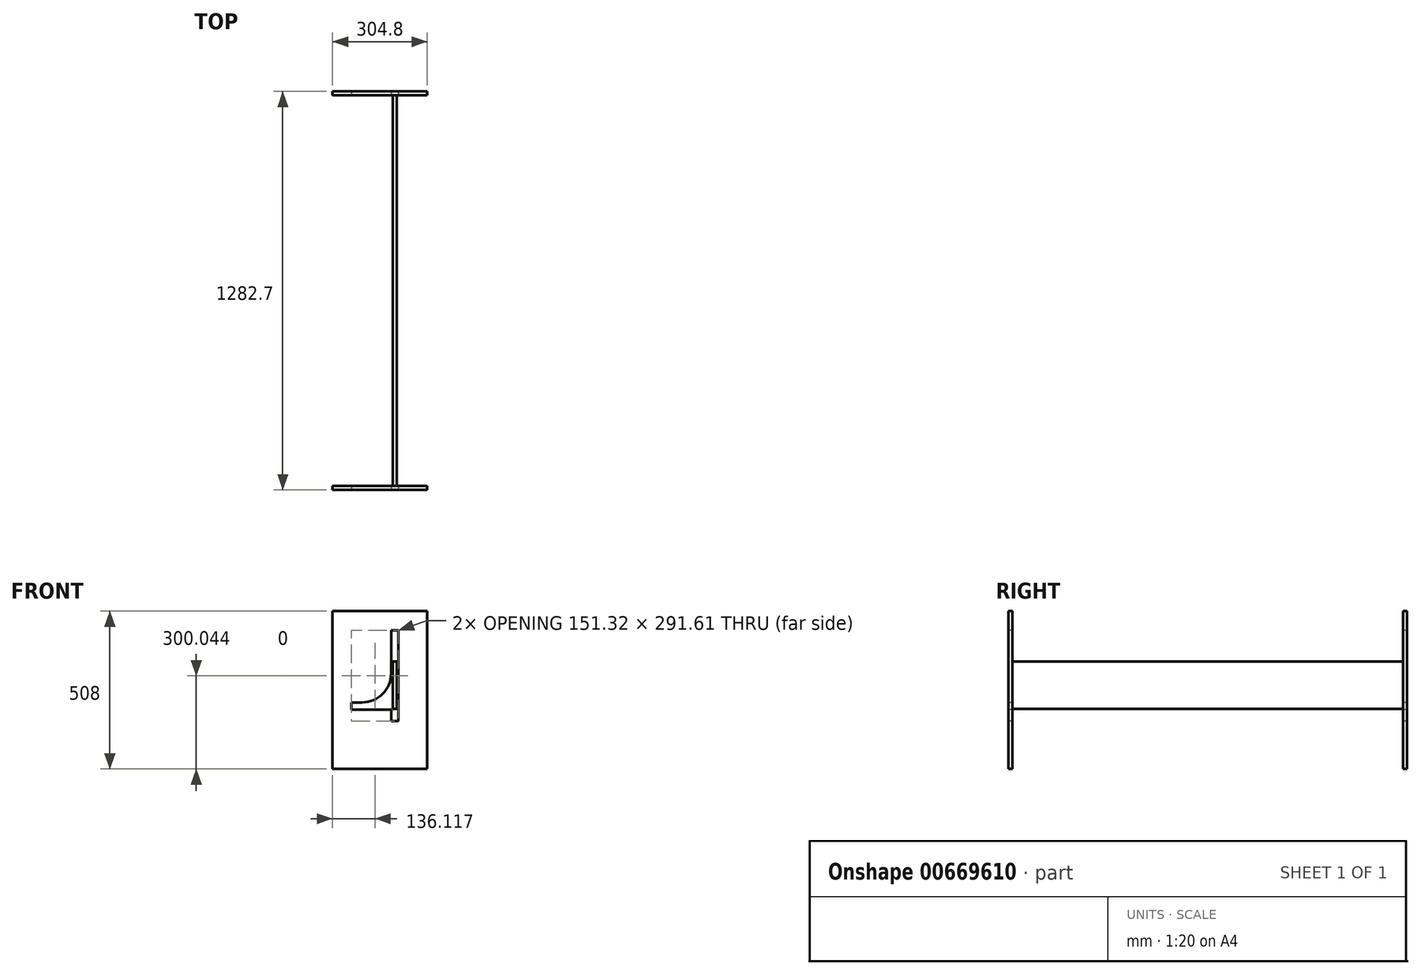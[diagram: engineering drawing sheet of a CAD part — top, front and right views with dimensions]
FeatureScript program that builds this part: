
annotation { "Feature Type Name" : "Feature", "Feature Type Description" : "" }
export const myFeature = defineFeature(function(context is Context, id is Id, definition is map)
    precondition{}
    {
        {
            var Q0;
            Q0=qCreatedBy(makeId("Front.planeOp"),FACE);
            var sketch = newSketch(context, id + "F0", { "sketchPlane" : qUnion([Q0])});
            skLineSegment(sketch, "E0.bottom", {"start": v(0, 0) * mm, "end": v(304.8, 0) * mm});
            skLineSegment(sketch, "E0.top", {"start": v(0, 508) * mm, "end": v(304.8, 508) * mm});
            skLineSegment(sketch, "E0.left", {"start": v(0, 0) * mm, "end": v(0, 508) * mm});
            skLineSegment(sketch, "E0.right", {"start": v(304.8, 0) * mm, "end": v(304.8, 508) * mm});
            skSolve(sketch);
        }
        {
            var Q0;
            Q0=makeQuery(id+"F0.imprint","IMPRINT",FACE,{"disambiguationData":[TD([[makeQuery(id+"F0.imprint","IMPRINT",EDGE,{"derivedFrom":sQuery(id+"F0.wireOp",EDGE,"E0.bottom")}),1.0]])]});
            extrude(context, id + "F1", {"entities" : qUnion([Q0]), "depth" : 12.7 * mm, "offsetDistance" : 25.4 * mm});
        }
        {
            var Q0;
            Q0=makeQuery(id+"F1.opExtrude","CAP_FACE",FACE,{"disambiguationData":[OSD([sQuery(id+"F0.wireOp",EDGE,"E0.bottom"),sQuery(id+"F0.wireOp",EDGE,"E0.top"),sQuery(id+"F0.wireOp",EDGE,"E0.left"),sQuery(id+"F0.wireOp",EDGE,"E0.right")])],"isStart":false});
            var sketch = newSketch(context, id + "F2", { "sketchPlane" : qUnion([Q0])});
            skLineSegment(sketch, "E1.bottom", {"start": v(188.63, 445.85) * mm, "end": v(211.78, 445.85) * mm});
            skLineSegment(sketch, "E1.top", {"start": v(188.63, 154.24) * mm, "end": v(211.78, 154.24) * mm});
            skLineSegment(sketch, "E1.right", {"start": v(211.78, 445.85) * mm, "end": v(211.78, 154.24) * mm});
            skLineSegment(sketch, "E2.top", {"start": v(188.63, 190.93) * mm, "end": v(60.46, 190.93) * mm});
            skLineSegment(sketch, "E2.right", {"start": v(60.46, 214.07) * mm, "end": v(60.46, 190.93) * mm});
            skLineSegment(sketch, "E3.trimOffspring", {"start": v(188.63, 190.93) * mm, "end": v(188.63, 154.24) * mm});
            skLineSegment(sketch, "E4", {"start": v(94.64, 214.07) * mm, "end": v(60.46, 214.07) * mm});
            skLineSegment(sketch, "E5", {"start": v(188.63, 308.07) * mm, "end": v(188.63, 445.85) * mm});
            skArc(sketch, "E6", {"start": v(94.64, 214.07) * mm, "mid": v(161.1, 241.6) * mm, "end": v(188.63, 308.07) * mm});
            skPoint(sketch, "E6.first.point", {"position": v(188.63, 308.07) * mm});
            skPoint(sketch, "E6.second.point", {"position": v(94.64, 214.07) * mm});
            skPoint(sketch, "E6.third.point", {"position": v(94.64, 402.06) * mm});
            skPoint(sketch, "E6.third.point.positionSnap0", {"position": v(94.64, 214.07) * mm});
            skPoint(sketch, "E7.orphan", {"position": v(128.82, 214.07) * mm});
            skSolve(sketch);
        }
        {
            var Q0;
            Q0=makeQuery(id+"F2.imprint","IMPRINT",FACE,{"disambiguationData":[TD([[makeQuery(id+"F2.imprint","IMPRINT",EDGE,{"derivedFrom":sQuery(id+"F2.wireOp",EDGE,"E1.bottom")}),-1.0]])]});
            extrude(context, id + "F3", {"entities" : qUnion([Q0]), "operationType" : NewBodyOperationType.REMOVE, "endBound" : BoundingType.THROUGH_ALL, "oppositeDirection" : true, "depth" : 25.4 * mm, "offsetDistance" : 25.4 * mm});
        }
        {
            var Q0;
            Q0=makeQuery(id+"F1.opExtrude","SWEPT_BODY",BODY,{"disambiguationData":[OSD([sQuery(id+"F0.wireOp",EDGE,"E0.bottom"),sQuery(id+"F0.wireOp",EDGE,"E0.top"),sQuery(id+"F0.wireOp",EDGE,"E0.left"),sQuery(id+"F0.wireOp",EDGE,"E0.right")])]});
            transform(context, id + "F4", {"entities" : qUnion([Q0]), "transformType" : TransformType.TRANSLATION_3D, "dx" : 0 * mm, "dy" : 1270 * mm, "dz" : 0 * mm, "makeCopy" : true});
        }
        {
            var Q0;
            Q0=makeQuery(id+"F4.opPattern","COPY",FACE,{"derivedFrom":makeQuery(id+"F1.opExtrude","CAP_FACE",FACE,{"disambiguationData":[OSD([sQuery(id+"F0.wireOp",EDGE,"E0.bottom"),sQuery(id+"F0.wireOp",EDGE,"E0.top"),sQuery(id+"F0.wireOp",EDGE,"E0.left"),sQuery(id+"F0.wireOp",EDGE,"E0.right")])],"isStart":false}),"instanceName":"1"});
            var sketch = newSketch(context, id + "F5", { "sketchPlane" : qUnion([Q0])});
            skLineSegment(sketch, "E8.bottom", {"start": v(193.45, 193.87) * mm, "end": v(206.15, 193.87) * mm});
            skLineSegment(sketch, "E8.top", {"start": v(193.45, 346.27) * mm, "end": v(206.15, 346.27) * mm});
            skLineSegment(sketch, "E8.left", {"start": v(193.45, 193.87) * mm, "end": v(193.45, 346.27) * mm});
            skLineSegment(sketch, "E8.right", {"start": v(206.15, 193.87) * mm, "end": v(206.15, 346.27) * mm});
            skSolve(sketch);
        }
        {
            var Q0;
            Q0 = qSketchRegion(id + "F5", true);
            var Q1;
            Q1=makeQuery(id+"F1.opExtrude","CAP_FACE",FACE,{"disambiguationData":[OSD([sQuery(id+"F0.wireOp",EDGE,"E0.bottom"),sQuery(id+"F0.wireOp",EDGE,"E0.top"),sQuery(id+"F0.wireOp",EDGE,"E0.left"),sQuery(id+"F0.wireOp",EDGE,"E0.right")])],"isStart":true});
            extrude(context, id + "F6", {"entities" : qUnion([Q0]), "endBound" : BoundingType.UP_TO_SURFACE, "depth" : 25.4 * mm, "endBoundEntityFace" : qUnion([Q1]), "offsetDistance" : 25.4 * mm});
        }
    });
